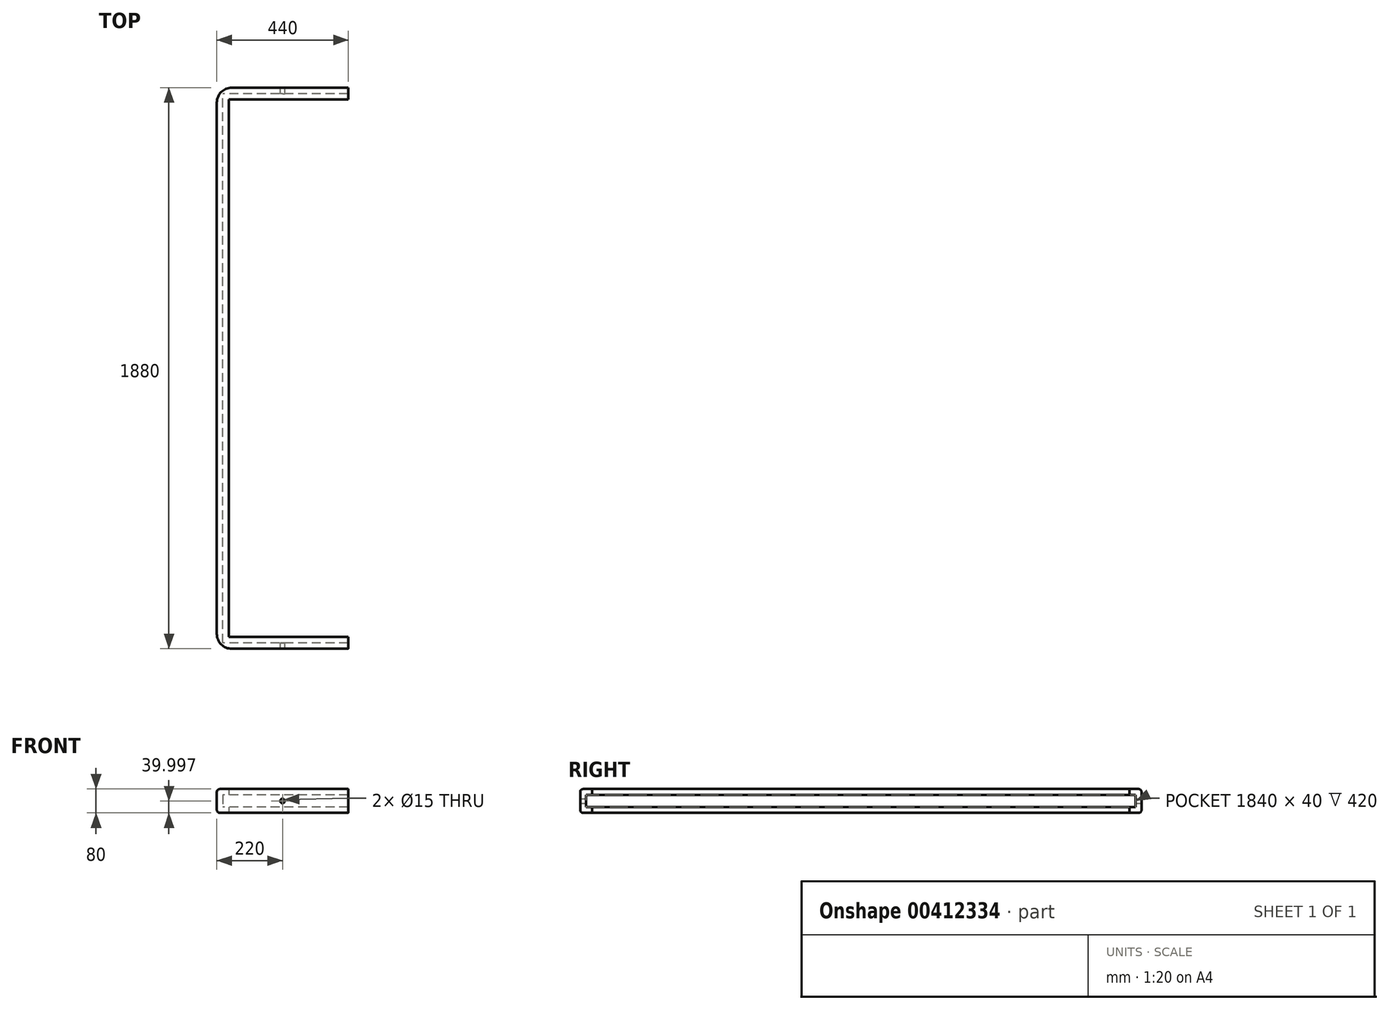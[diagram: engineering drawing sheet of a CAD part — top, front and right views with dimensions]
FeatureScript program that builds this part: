
annotation { "Feature Type Name" : "Feature", "Feature Type Description" : "" }
export const myFeature = defineFeature(function(context is Context, id is Id, definition is map)
    precondition{}
    {
        {
            var Q0;
            Q0=qCreatedBy(makeId("Right.planeOp"),FACE);
            var sketch = newSketch(context, id + "F0", { "sketchPlane" : qUnion([Q0])});
            skLineSegment(sketch, "E0.bottom", {"start": v(-121.69, 25.3) * mm, "end": v(1758.31, 25.3) * mm});
            skLineSegment(sketch, "E0.top", {"start": v(-121.69, -54.7) * mm, "end": v(1758.31, -54.7) * mm});
            skLineSegment(sketch, "E0.left", {"start": v(-121.69, 25.3) * mm, "end": v(-121.69, -54.7) * mm});
            skLineSegment(sketch, "E0.right", {"start": v(1758.31, 25.3) * mm, "end": v(1758.31, -54.7) * mm});
            skSolve(sketch);
        }
        {
            var Q0;
            Q0 = qSketchRegion(id + "F0", true);
            extrude(context, id + "F1", {"entities" : qUnion([Q0]), "depth" : 440 * mm});
        }
        {
            var Q0;
            Q0=makeQuery(id+"F1.opExtrude","CAP_FACE",FACE,{"disambiguationData":[OSD([sQuery(id+"F0.wireOp",EDGE,"E0.bottom"),sQuery(id+"F0.wireOp",EDGE,"E0.top"),sQuery(id+"F0.wireOp",EDGE,"E0.left"),sQuery(id+"F0.wireOp",EDGE,"E0.right")])],"isStart":false});
            var sketch = newSketch(context, id + "F2", { "sketchPlane" : qUnion([Q0])});
            skLineSegment(sketch, "E1", {"start": v(-121.69, 25.3) * mm, "end": v(-81.69, 25.3) * mm, "construction": true});
            skLineSegment(sketch, "E2.bottom", {"start": v(-81.69, 25.3) * mm, "end": v(1718.31, 25.3) * mm});
            skLineSegment(sketch, "E2.top", {"start": v(-81.69, -54.7) * mm, "end": v(1718.31, -54.7) * mm});
            skLineSegment(sketch, "E2.left", {"start": v(-81.69, 25.3) * mm, "end": v(-81.69, -54.7) * mm});
            skLineSegment(sketch, "E2.right", {"start": v(1718.31, 25.3) * mm, "end": v(1718.31, -54.7) * mm});
            skSolve(sketch);
        }
        {
            var Q0;
            Q0 = qSketchRegion(id + "F2", true);
            extrude(context, id + "F3", {"entities" : qUnion([Q0]), "operationType" : NewBodyOperationType.REMOVE, "oppositeDirection" : true, "depth" : 400 * mm});
        }
        {
            var Q0;
            Q0=makeQuery(id+"F3.boolean.opBoolean","COPY",FACE,{"derivedFrom":makeQuery(id+"F3.opExtrude","SWEPT_FACE",FACE,{"disambiguationData":[OSD([sQuery(id+"F2.wireOp",EDGE,"E2.right")])]})});
            var sketch = newSketch(context, id + "F4", { "sketchPlane" : qUnion([Q0])});
            skLineSegment(sketch, "E3.bottom", {"start": v(440, -34.7) * mm, "end": v(40, -34.7) * mm});
            skLineSegment(sketch, "E3.top", {"start": v(440, 5.3) * mm, "end": v(40, 5.3) * mm});
            skLineSegment(sketch, "E3.left", {"start": v(440, -34.7) * mm, "end": v(440, 5.3) * mm});
            skLineSegment(sketch, "E3.right", {"start": v(40, -34.7) * mm, "end": v(40, 5.3) * mm});
            skLineSegment(sketch, "E4", {"start": v(440, -34.7) * mm, "end": v(440, -54.7) * mm, "construction": true});
            skSolve(sketch);
        }
        {
            var Q0;
            Q0 = qSketchRegion(id + "F4", true);
            extrude(context, id + "F5", {"entities" : qUnion([Q0]), "operationType" : NewBodyOperationType.REMOVE, "oppositeDirection" : true, "depth" : 20 * mm});
        }
        {
            var Q0;
            Q0=makeQuery(id+"F3.boolean.opBoolean","COPY",FACE,{"derivedFrom":makeQuery(id+"F3.opExtrude","SWEPT_FACE",FACE,{"disambiguationData":[OSD([sQuery(id+"F2.wireOp",EDGE,"E2.left")])]})});
            var sketch = newSketch(context, id + "F6", { "sketchPlane" : qUnion([Q0])});
            skLineSegment(sketch, "E5.bottom", {"start": v(-440, -34.7) * mm, "end": v(-40, -34.7) * mm});
            skLineSegment(sketch, "E5.top", {"start": v(-440, 5.3) * mm, "end": v(-40, 5.3) * mm});
            skLineSegment(sketch, "E5.left", {"start": v(-440, -34.7) * mm, "end": v(-440, 5.3) * mm});
            skLineSegment(sketch, "E5.right", {"start": v(-40, -34.7) * mm, "end": v(-40, 5.3) * mm});
            skLineSegment(sketch, "E6", {"start": v(-440, -34.7) * mm, "end": v(-440, -54.7) * mm, "construction": true});
            skSolve(sketch);
        }
        {
            var Q0;
            Q0 = qSketchRegion(id + "F6", true);
            extrude(context, id + "F7", {"entities" : qUnion([Q0]), "operationType" : NewBodyOperationType.REMOVE, "oppositeDirection" : true, "depth" : 20 * mm});
        }
        {
            var Q0;
            Q0=makeQuery(id+"F7.boolean.opBoolean","MERGE",FACE,{"derivedFrom":[makeQuery(id+"F5.boolean.opBoolean","MERGE",FACE,{"derivedFrom":[makeQuery(id+"F3.boolean.opBoolean","COPY",FACE,{"derivedFrom":makeQuery(id+"F3.opExtrude","CAP_FACE",FACE,{"disambiguationData":[OSD([sQuery(id+"F2.wireOp",EDGE,"E2.bottom"),sQuery(id+"F2.wireOp",EDGE,"E2.top"),sQuery(id+"F2.wireOp",EDGE,"E2.left"),sQuery(id+"F2.wireOp",EDGE,"E2.right")])],"isStart":false})}),makeQuery(id+"F5.opExtrude","SWEPT_FACE",FACE,{"disambiguationData":[OSD([sQuery(id+"F4.wireOp",EDGE,"E3.right")])]})]}),makeQuery(id+"F7.opExtrude","SWEPT_FACE",FACE,{"disambiguationData":[OSD([sQuery(id+"F6.wireOp",EDGE,"E5.right")])]})]});
            var sketch = newSketch(context, id + "F8", { "sketchPlane" : qUnion([Q0])});
            skLineSegment(sketch, "E7.bottom", {"start": v(-101.69, 5.3) * mm, "end": v(1738.31, 5.3) * mm});
            skLineSegment(sketch, "E7.top", {"start": v(-101.69, -34.7) * mm, "end": v(1738.31, -34.7) * mm});
            skLineSegment(sketch, "E7.left", {"start": v(-101.69, 5.3) * mm, "end": v(-101.69, -34.7) * mm});
            skLineSegment(sketch, "E7.right", {"start": v(1738.31, 5.3) * mm, "end": v(1738.31, -34.7) * mm});
            skSolve(sketch);
        }
        {
            var Q0;
            Q0 = qSketchRegion(id + "F8", true);
            extrude(context, id + "F9", {"entities" : qUnion([Q0]), "operationType" : NewBodyOperationType.REMOVE, "oppositeDirection" : true, "depth" : 20 * mm});
        }
        {
            var Q0;
            Q0=makeQuery(id+"F1.opExtrude","SWEPT_FACE",FACE,{"disambiguationData":[OSD([sQuery(id+"F0.wireOp",EDGE,"E0.right")])]});
            var sketch = newSketch(context, id + "F10", { "sketchPlane" : qUnion([Q0])});
            skLineSegment(sketch, "E8", {"start": v(-440, -14.7) * mm, "end": v(0, -14.7) * mm, "construction": true});
            skLineSegment(sketch, "E9", {"start": v(-220, -54.7) * mm, "end": v(-220, 25.3) * mm, "construction": true});
            skPoint(sketch, "E10", {"position": v(-220, -14.7) * mm});
            skSolve(sketch);
        }
        {
            var Q0;
            Q0=sQuery(id+"F10.wireOp",VERTEX,"E10");
            var Q1;
            Q1=makeQuery(id+"F1.opExtrude","SWEPT_BODY",BODY,{"disambiguationData":[OSD([sQuery(id+"F0.wireOp",EDGE,"E0.bottom"),sQuery(id+"F0.wireOp",EDGE,"E0.top"),sQuery(id+"F0.wireOp",EDGE,"E0.left"),sQuery(id+"F0.wireOp",EDGE,"E0.right")])]});
            hole(context, id + "F11", {"style" : HoleStyle.SIMPLE, "endStyle" : HoleEndStyle.THROUGH, "holeDiameter" : 15 * mm, "isTappedThrough" : true, "tappedDepth" : 12 * mm, "tapClearance" : 3, "startFromSketch" : true, "locations" : qUnion([Q0]), "scope" : qUnion([Q1])});
        }
        {
            var Q0;
            Q0=makeQuery(id+"F1.opExtrude","CAP_EDGE",EDGE,{"disambiguationData":[OSD([sQuery(id+"F0.wireOp",EDGE,"E0.right")])],"isStart":true});
            fillet(context, id + "F12", {"entities" : qUnion([Q0]), "radius" : 50 * mm, "tangentPropagation" : true, "allowEdgeOverflow" : false});
        }
        {
            var Q0;
            Q0=makeQuery(id+"F1.opExtrude","CAP_EDGE",EDGE,{"disambiguationData":[OSD([sQuery(id+"F0.wireOp",EDGE,"E0.left")])],"isStart":true});
            fillet(context, id + "F13", {"entities" : qUnion([Q0]), "radius" : 50 * mm, "tangentPropagation" : true, "allowEdgeOverflow" : false});
        }
        {
            var Q0;
            Q0=makeQuery(id+"F1.opExtrude","CAP_EDGE",EDGE,{"disambiguationData":[OSD([sQuery(id+"F0.wireOp",EDGE,"E0.top")])],"isStart":true});
            var Q1;
            Q1=makeQuery(id+"F1.opExtrude","CAP_EDGE",EDGE,{"disambiguationData":[OSD([sQuery(id+"F0.wireOp",EDGE,"E0.bottom")])],"isStart":true});
            fillet(context, id + "F14", {"entities" : qUnion([Q0, Q1]), "radius" : 10 * mm, "tangentPropagation" : true, "allowEdgeOverflow" : false});
        }
    });
